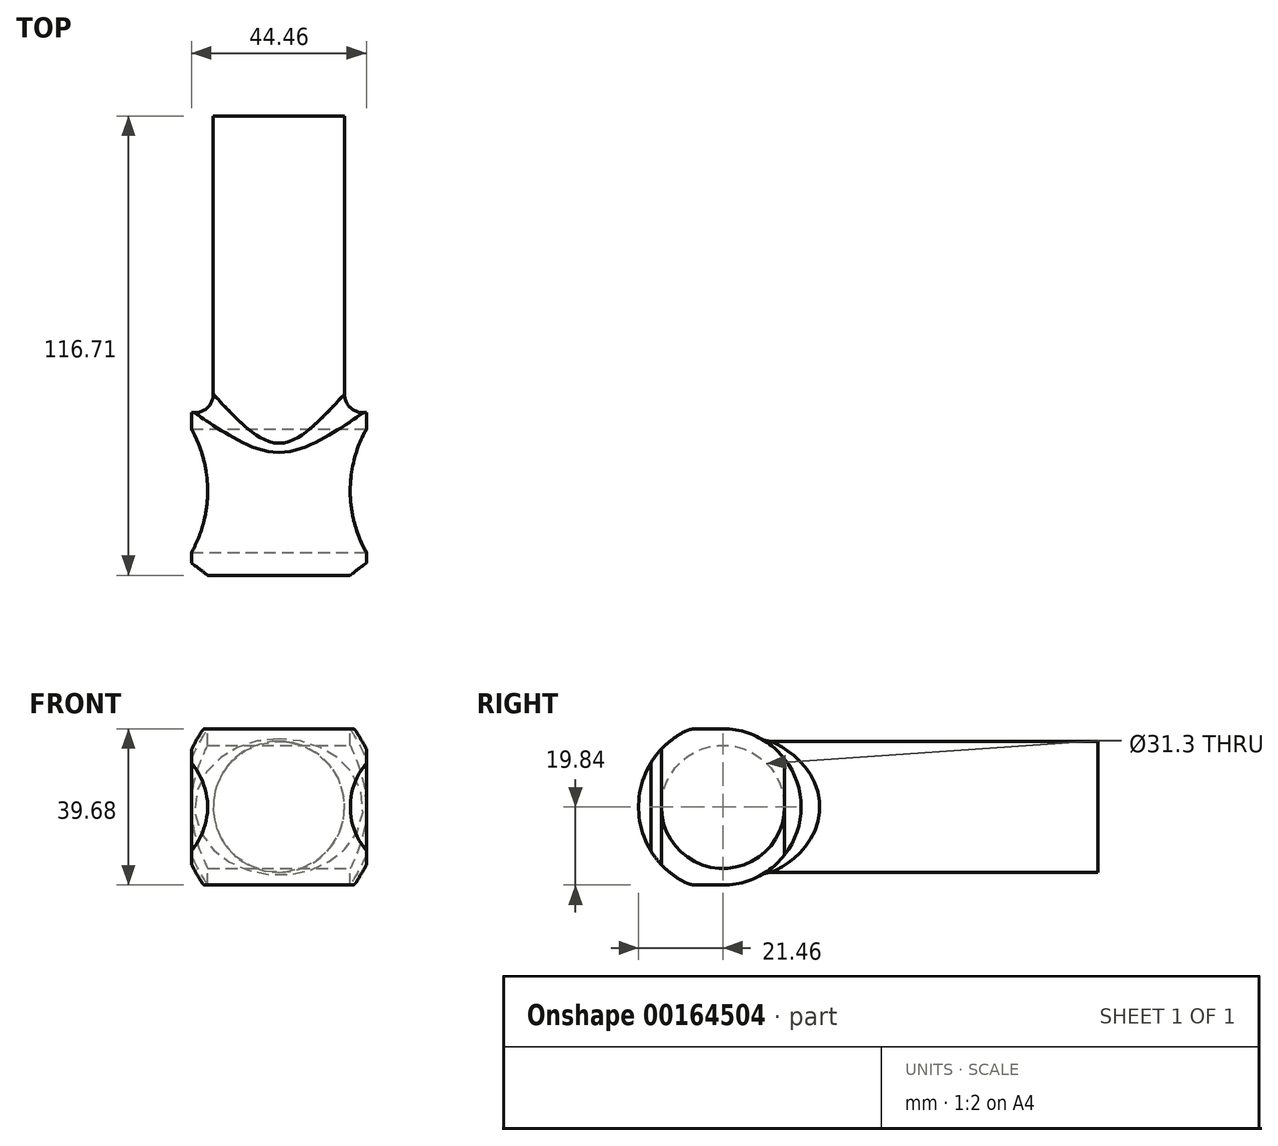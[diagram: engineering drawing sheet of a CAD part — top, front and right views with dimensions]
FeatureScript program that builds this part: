
annotation { "Feature Type Name" : "Feature", "Feature Type Description" : "" }
export const myFeature = defineFeature(function(context is Context, id is Id, definition is map)
    precondition{}
    {
        {
            var Q0;
            Q0=qCreatedBy(makeId("Front.planeOp"),FACE);
            var sketch = newSketch(context, id + "F0", { "sketchPlane" : qUnion([Q0])});
            skCircle(sketch, "E0", {"center": v(0, 0) * mm, "radius": 16.67 * mm});
            skSolve(sketch);
        }
        {
            var Q0;
            Q0=makeQuery(id+"F0.imprint","IMPRINT",FACE,{"disambiguationData":[TD([[makeQuery(id+"F0.imprint","IMPRINT",EDGE,{"derivedFrom":sQuery(id+"F0.wireOp",EDGE,"E0")}),1.0]])]});
            extrude(context, id + "F1", {"entities" : qUnion([Q0]), "endBound" : BoundingType.SYMMETRIC, "depth" : 127 * mm});
        }
        {
            var Q0;
            Q0=qCreatedBy(makeId("Right.planeOp"),FACE);
            var sketch = newSketch(context, id + "F2", { "sketchPlane" : qUnion([Q0])});
            skCircle(sketch, "E1", {"center": v(-31.75, 0) * mm, "radius": 19.84 * mm, "construction": true});
            skArc(sketch, "E2", {"start": v(-39.91, 19.84) * mm, "mid": v(-53.2, 0) * mm, "end": v(-39.91, -19.84) * mm});
            skArc(sketch, "E3", {"start": v(-31.75, -19.84) * mm, "mid": v(-11.9, 0) * mm, "end": v(-31.75, 19.84) * mm});
            skLineSegment(sketch, "E4", {"start": v(-31.75, 19.84) * mm, "end": v(-31.75, -19.84) * mm, "construction": true});
            skLineSegment(sketch, "E5", {"start": v(-31.75, 19.84) * mm, "end": v(-39.91, 19.84) * mm});
            skLineSegment(sketch, "E6", {"start": v(-31.75, -19.84) * mm, "end": v(-39.91, -19.84) * mm});
            skCircle(sketch, "E7", {"center": v(-31.75, 0) * mm, "radius": 15.9 * mm, "construction": true});
            skSolve(sketch);
        }
        {
            var Q0;
            Q0 = qSketchRegion(id + "F2", true);
            extrude(context, id + "F3", {"entities" : qUnion([Q0]), "operationType" : NewBodyOperationType.ADD, "endBound" : BoundingType.SYMMETRIC, "depth" : 44.45 * mm});
        }
        {
            var Q0;
            Q0=qCreatedBy(makeId("Right.planeOp"),FACE);
            var sketch = newSketch(context, id + "F4", { "sketchPlane" : qUnion([Q0])});
            skPoint(sketch, "E8.0", {"position": v(-31.75, 0) * mm});
            skCircle(sketch, "E9", {"center": v(-31.75, 0) * mm, "radius": 15.65 * mm});
            skArc(sketch, "E10.0", {"start": v(-39.91, 19.84) * mm, "mid": v(-53.2, 0) * mm, "end": v(-39.91, -19.84) * mm});
            skLineSegment(sketch, "E11", {"start": v(-39.91, 19.84) * mm, "end": v(-65.31, 19.84) * mm});
            skLineSegment(sketch, "E12", {"start": v(-65.31, 19.84) * mm, "end": v(-65.31, -19.84) * mm});
            skLineSegment(sketch, "E13", {"start": v(-65.31, -19.84) * mm, "end": v(-39.91, -19.84) * mm});
            skSolve(sketch);
        }
        {
            var Q0;
            Q0 = qSketchRegion(id + "F4", true);
            extrude(context, id + "F5", {"entities" : qUnion([Q0]), "operationType" : NewBodyOperationType.REMOVE, "endBound" : BoundingType.THROUGH_ALL, "oppositeDirection" : true, "depth" : 25.4 * mm, "hasSecondDirection" : true, "secondDirectionBound" : SecondDirectionBoundingType.THROUGH_ALL, "secondDirectionOppositeDirection" : false, "secondDirectionDepth" : 25.4 * mm});
        }
        {
            var Q0;
            Q0=makeQuery(id+"F3.boolean.opBoolean","INTERSECT",EDGE,{"derivedFrom":[makeQuery(id+"F1.opExtrude","SWEPT_FACE",FACE,{"disambiguationData":[OSD([sQuery(id+"F0.wireOp",EDGE,"E0")])]}),makeQuery(id+"F3.opExtrude","SWEPT_FACE",FACE,{"disambiguationData":[OSD([sQuery(id+"F2.wireOp",EDGE,"E3")])]})]});
            fillet(context, id + "F6", {"entities" : qUnion([Q0]), "radius" : 4.76 * mm, "tangentPropagation" : true, "allowEdgeOverflow" : false});
        }
        {
            var Q0;
            Q0=qCreatedBy(makeId("Top.planeOp"),FACE);
            var sketch = newSketch(context, id + "F7", { "sketchPlane" : qUnion([Q0])});
            skLineSegment(sketch, "E14.0", {"start": v(0, -11.9) * mm, "end": v(0, -51.6) * mm, "construction": true});
            skLineSegment(sketch, "E15.0", {"start": v(-22.22, -47.4) * mm, "end": v(-22.22, -16.1) * mm});
            skArc(sketch, "E16", {"start": v(-22.22, -47.4) * mm, "mid": v(-18.1, -31.75) * mm, "end": v(-22.22, -16.1) * mm});
            skLineSegment(sketch, "E17.MirrorCS", {"start": v(22.22, -16.1) * mm, "end": v(22.22, -47.4) * mm});
            skArc(sketch, "E18.MirrorCS", {"start": v(22.22, -47.4) * mm, "mid": v(18.1, -31.75) * mm, "end": v(22.22, -16.1) * mm});
            skLineSegment(sketch, "E19", {"start": v(22.22, -50.03) * mm, "end": v(18.1, -53.2) * mm});
            skLineSegment(sketch, "E20", {"start": v(18.1, -53.2) * mm, "end": v(18.1, -9.22) * mm, "construction": true});
            skPoint(sketch, "E21.0", {"position": v(22.23, -53.2) * mm});
            skLineSegment(sketch, "E22", {"start": v(18.1, -53.2) * mm, "end": v(22.23, -53.2) * mm});
            skPoint(sketch, "E23.MirrorP", {"position": v(-22.23, -53.2) * mm});
            skLineSegment(sketch, "E24.MirrorCS", {"start": v(-22.22, -50.03) * mm, "end": v(-18.1, -53.2) * mm});
            skLineSegment(sketch, "E25.MirrorCS", {"start": v(-18.1, -53.2) * mm, "end": v(-22.23, -53.2) * mm});
            skLineSegment(sketch, "E26", {"start": v(22.22, -50.03) * mm, "end": v(22.22, -53.2) * mm});
            skLineSegment(sketch, "E27", {"start": v(-22.22, -50.03) * mm, "end": v(-22.22, -53.2) * mm});
            skSolve(sketch);
        }
        {
            var Q0;
            Q0 = qSketchRegion(id + "F7", true);
            extrude(context, id + "F8", {"entities" : qUnion([Q0]), "operationType" : NewBodyOperationType.REMOVE, "endBound" : BoundingType.THROUGH_ALL, "oppositeDirection" : true, "depth" : 25.4 * mm, "hasSecondDirection" : true, "secondDirectionBound" : SecondDirectionBoundingType.THROUGH_ALL, "secondDirectionOppositeDirection" : false, "secondDirectionDepth" : 25.4 * mm});
        }
        {
            var Q0;
            Q0=makeQuery(id+"F3.opExtrude","SWEPT_EDGE",EDGE,{"disambiguationData":[OSD([sQuery(id+"F2.wireOp",EDGE,"E2"),sQuery(id+"F2.wireOp",EDGE,"E5")])]});
            var Q1;
            Q1=makeQuery(id+"F3.opExtrude","SWEPT_EDGE",EDGE,{"disambiguationData":[OSD([sQuery(id+"F2.wireOp",EDGE,"E2"),sQuery(id+"F2.wireOp",EDGE,"E6")])]});
            fillet(context, id + "F9", {"entities" : qUnion([Q0, Q1]), "radius" : 6.35 * mm, "tangentPropagation" : true, "allowEdgeOverflow" : false});
        }
    });
